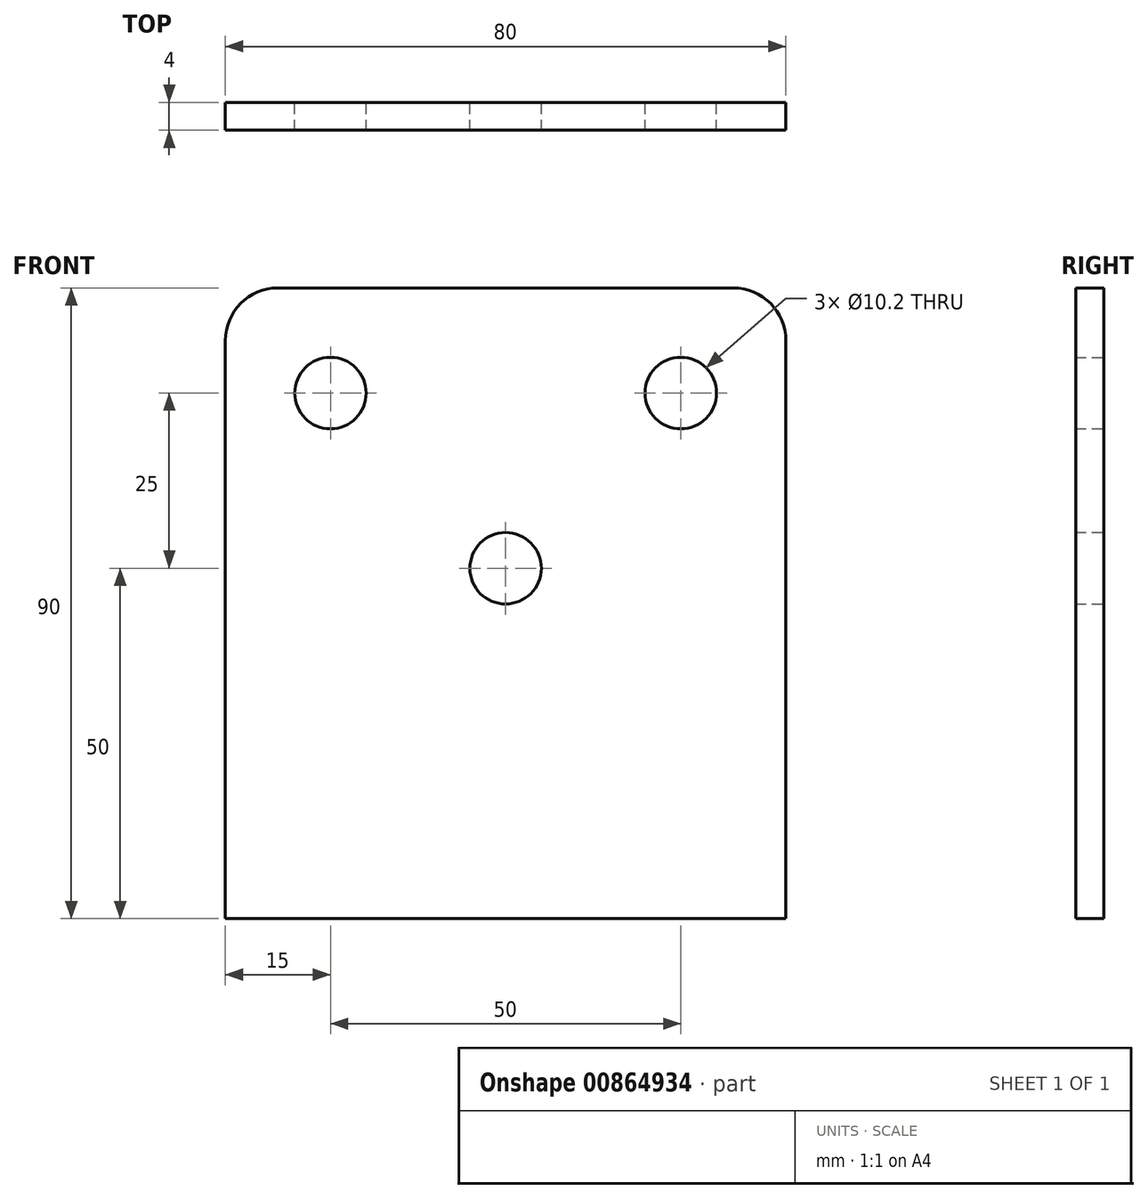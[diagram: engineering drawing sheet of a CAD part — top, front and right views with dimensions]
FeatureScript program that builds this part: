
annotation { "Feature Type Name" : "Feature", "Feature Type Description" : "" }
export const myFeature = defineFeature(function(context is Context, id is Id, definition is map)
    precondition{}
    {
        {
            var Q0;
            Q0=qCreatedBy(makeId("Front.planeOp"),FACE);
            var sketch = newSketch(context, id + "F0", { "sketchPlane" : qUnion([Q0])});
            skLineSegment(sketch, "E0.bottom", {"start": v(32.5, 45) * mm, "end": v(-32.5, 45) * mm});
            skLineSegment(sketch, "E0.top", {"start": v(40, -45) * mm, "end": v(-40, -45) * mm});
            skLineSegment(sketch, "E0.left", {"start": v(40, 37.5) * mm, "end": v(40, -45) * mm});
            skLineSegment(sketch, "E0.right", {"start": v(-40, 37.5) * mm, "end": v(-40, -45) * mm});
            skPoint(sketch, "E0.middle", {"position": v(0, 0) * mm});
            skCircle(sketch, "E1", {"center": v(-25, 30) * mm, "radius": 5.1 * mm});
            skCircle(sketch, "E2", {"center": v(25, 30) * mm, "radius": 5.1 * mm});
            skCircle(sketch, "E3", {"center": v(0, 5) * mm, "radius": 5.1 * mm});
            skPoint(sketch, "E4.visualSharp", {"position": v(-40, 45) * mm});
            skArc(sketch, "E4.filletArc", {"start": v(-32.5, 45) * mm, "mid": v(-37.8, 42.8) * mm, "end": v(-40, 37.5) * mm});
            skPoint(sketch, "E5.visualSharp", {"position": v(40, 45) * mm});
            skArc(sketch, "E5.filletArc", {"start": v(40, 37.5) * mm, "mid": v(37.8, 42.8) * mm, "end": v(32.5, 45) * mm});
            skSolve(sketch);
        }
        {
            var Q0;
            Q0 = qSketchRegion(id + "F0", true);
            extrude(context, id + "F1", {"entities" : qUnion([Q0]), "depth" : 4 * mm, "offsetDistance" : 25 * mm});
        }
    });
